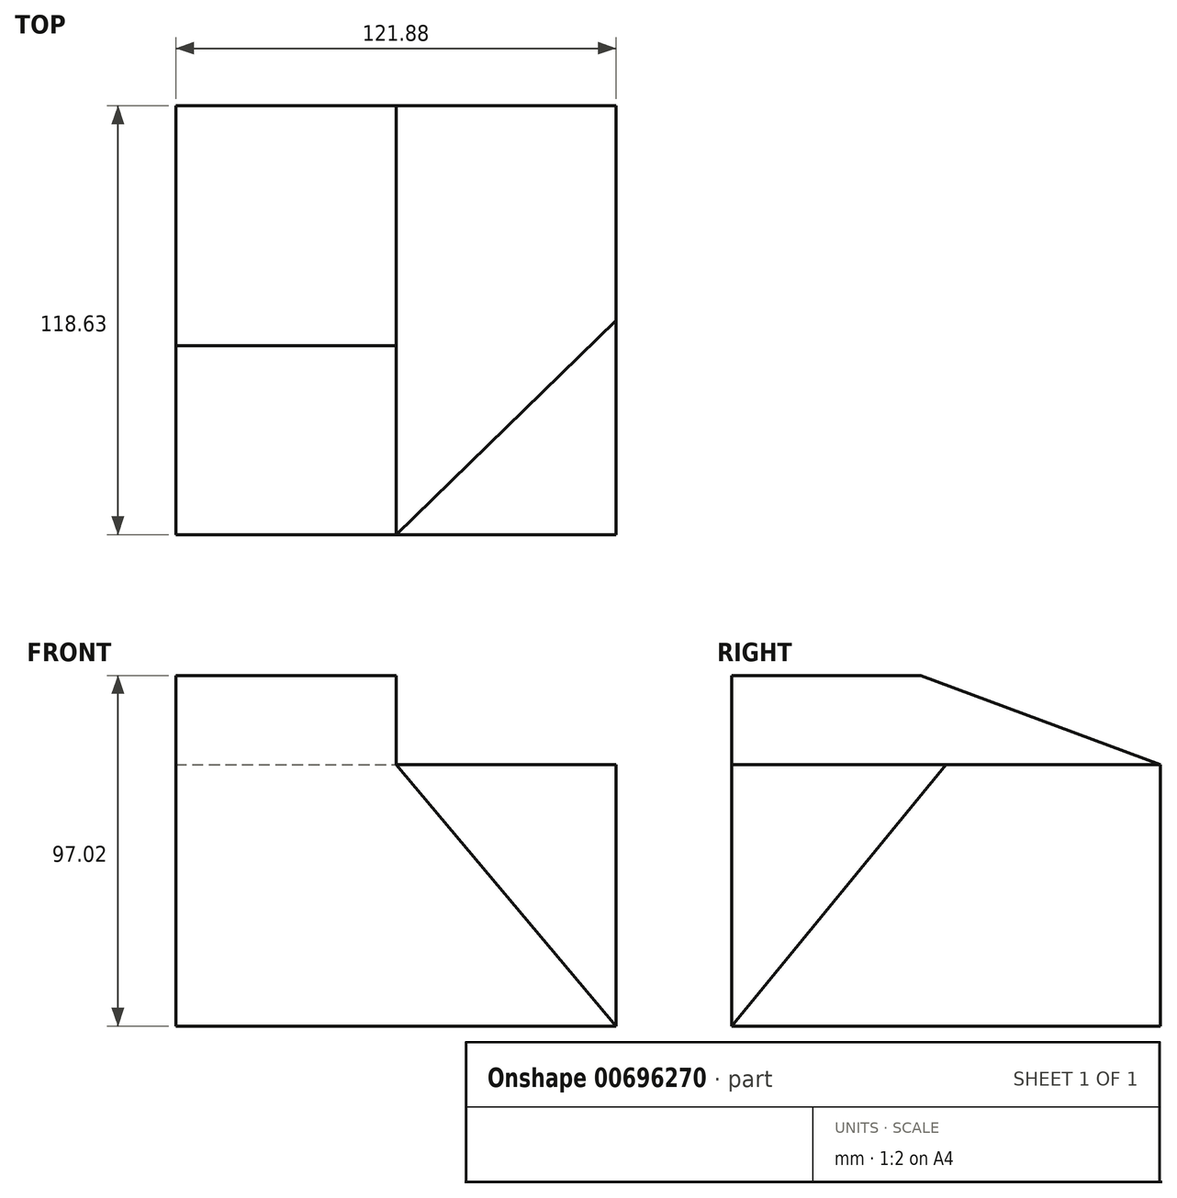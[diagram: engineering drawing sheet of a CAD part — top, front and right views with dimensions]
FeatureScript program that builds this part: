
annotation { "Feature Type Name" : "Feature", "Feature Type Description" : "" }
export const myFeature = defineFeature(function(context is Context, id is Id, definition is map)
    precondition{}
    {
        {
            var Q0;
            Q0=qCreatedBy(makeId("Top.planeOp"),FACE);
            var sketch = newSketch(context, id + "F0", { "sketchPlane" : qUnion([Q0])});
            skLineSegment(sketch, "E0.bottom", {"start": v(-59.8, -52.29) * mm, "end": v(62.08, -52.29) * mm});
            skLineSegment(sketch, "E0.top", {"start": v(-59.8, 66.34) * mm, "end": v(62.08, 66.34) * mm});
            skLineSegment(sketch, "E0.left", {"start": v(-59.8, -52.29) * mm, "end": v(-59.8, 66.34) * mm});
            skLineSegment(sketch, "E0.right", {"start": v(62.08, -52.29) * mm, "end": v(62.08, 66.34) * mm});
            skSolve(sketch);
        }
        {
            var Q0;
            Q0=makeQuery(id+"F0.imprint","IMPRINT",FACE,{"disambiguationData":[TD([[makeQuery(id+"F0.imprint","IMPRINT",EDGE,{"derivedFrom":sQuery(id+"F0.wireOp",EDGE,"E0.bottom")}),1.0]])]});
            extrude(context, id + "F1", {"entities" : qUnion([Q0]), "depth" : 72.39 * mm, "offsetDistance" : 25.4 * mm});
        }
        {
            var Q0;
            Q0=makeQuery(id+"F1.opExtrude","SWEPT_FACE",FACE,{"disambiguationData":[OSD([sQuery(id+"F0.wireOp",EDGE,"E0.left")])]});
            var sketch = newSketch(context, id + "F2", { "sketchPlane" : qUnion([Q0])});
            skLineSegment(sketch, "E1", {"start": v(52.29, 72.39) * mm, "end": v(52.29, 97.02) * mm});
            skLineSegment(sketch, "E2", {"start": v(52.29, 97.02) * mm, "end": v(0, 97.02) * mm});
            skLineSegment(sketch, "E3", {"start": v(0, 97.02) * mm, "end": v(-66.34, 72.39) * mm});
            skSolve(sketch);
        }
        {
            var Q0;
            Q0=makeQuery(id+"F2.imprint","IMPRINT",FACE,{"disambiguationData":[TD([[makeQuery(id+"F2.imprint","IMPRINT",EDGE,{"derivedFrom":sQuery(id+"F2.wireOp",EDGE,"E1")}),1.0]])]});
            extrude(context, id + "F3", {"entities" : qUnion([Q0]), "operationType" : NewBodyOperationType.ADD, "oppositeDirection" : true, "depth" : 60.96 * mm, "offsetDistance" : 25.4 * mm});
        }
        {
            var Q0;
            Q0=makeQuery(id+"F1.opExtrude","CAP_EDGE",EDGE,{"disambiguationData":[OSD([sQuery(id+"F0.wireOp",EDGE,"E0.right")])],"isStart":false});
            cPoint(context, id + "F4", {"entities" : qUnion([Q0]), "parameter" : 0.5});
        }
        {
            var Q0;
            Q0=makeQuery(id+"F3.opExtrude","CAP_VERTEX",VERTEX,{"disambiguationData":[OSD([sQuery(id+"F0.wireOp",EDGE,"E0.bottom"),sQuery(id+"F0.wireOp",EDGE,"E0.left"),sQuery(id+"F2.wireOp",EDGE,"E1")])],"isStart":false});
            var Q1;
            Q1=makeQuery(id+"F1.opExtrude","CAP_VERTEX",VERTEX,{"disambiguationData":[OSD([sQuery(id+"F0.wireOp",EDGE,"E0.bottom"),sQuery(id+"F0.wireOp",EDGE,"E0.right")])],"isStart":true});
            var Q2;
            Q2 = qCreatedBy(id + "F4" ,VERTEX);
            cPlane(context, id + "F5", {"entities" : qUnion([Q0, Q1, Q2]), "cplaneType" : CPlaneType.THREE_POINT, "offset" : 25.4 * mm, "width" : 152.4 * mm, "height" : 152.4 * mm});
        }
        {
            var Q0;
            Q0=qCreatedBy(id+"F5.planeOp",FACE);
            var sketch = newSketch(context, id + "F6", { "sketchPlane" : qUnion([Q0])});
            skLineSegment(sketch, "E4", {"start": v(-25.26, -33.14) * mm, "end": v(-25.26, 60.45) * mm});
            skLineSegment(sketch, "E5", {"start": v(51, 22.85) * mm, "end": v(-25.26, 60.45) * mm});
            skLineSegment(sketch, "E6", {"start": v(51, 22.85) * mm, "end": v(-25.26, -33.14) * mm});
            skLineSegment(sketch, "E7", {"start": v(76.95, 41.9) * mm, "end": v(51, 22.85) * mm});
            skSolve(sketch);
        }
        {
            var Q0;
            Q0=makeQuery(id+"F6.imprint","IMPRINT",FACE,{"disambiguationData":[TD([[makeQuery(id+"F6.imprint","IMPRINT",EDGE,{"derivedFrom":sQuery(id+"F6.wireOp",EDGE,"E4")}),-1.0]])]});
            extrude(context, id + "F7", {"entities" : qUnion([Q0]), "operationType" : NewBodyOperationType.REMOVE, "endBound" : BoundingType.THROUGH_ALL, "oppositeDirection" : true, "depth" : 207.77 * mm, "offsetDistance" : 25.4 * mm});
        }
    });
